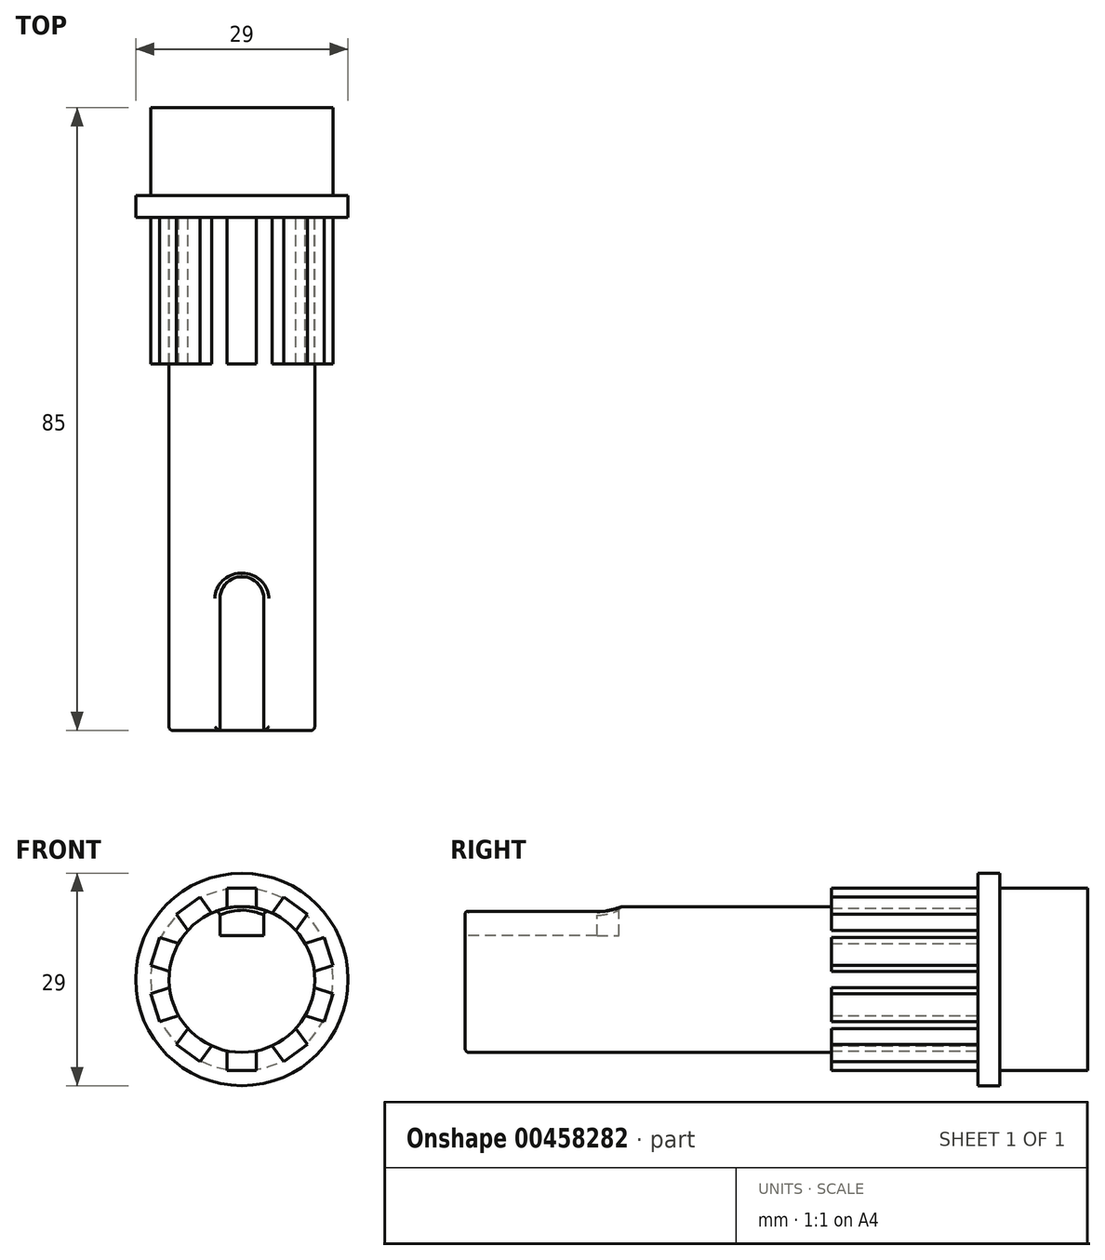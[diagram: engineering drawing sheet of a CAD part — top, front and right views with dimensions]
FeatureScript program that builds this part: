
annotation { "Feature Type Name" : "Feature", "Feature Type Description" : "" }
export const myFeature = defineFeature(function(context is Context, id is Id, definition is map)
    precondition{}
    {
        {
            var Q0;
            Q0=qCreatedBy(makeId("Front.planeOp"),FACE);
            var sketch = newSketch(context, id + "F0", { "sketchPlane" : qUnion([Q0])});
            skCircle(sketch, "E0", {"center": v(0, 0) * mm, "radius": 12.45 * mm});
            skSolve(sketch);
        }
        {
            var Q0;
            Q0=makeQuery(id+"F0.imprint","IMPRINT",FACE,{"disambiguationData":[TD([[makeQuery(id+"F0.imprint","IMPRINT",EDGE,{"derivedFrom":sQuery(id+"F0.wireOp",EDGE,"E0")}),1.0]])]});
            extrude(context, id + "F1", {"entities" : qUnion([Q0]), "oppositeDirection" : true, "depth" : 12 * mm, "offsetDistance" : 25 * mm});
        }
        {
            var Q0;
            Q0=qCreatedBy(makeId("Front.planeOp"),FACE);
            var sketch = newSketch(context, id + "F2", { "sketchPlane" : qUnion([Q0])});
            skCircle(sketch, "E1", {"center": v(0, 0) * mm, "radius": 14.5 * mm});
            skSolve(sketch);
        }
        {
            var Q0;
            Q0=makeQuery(id+"F2.imprint","IMPRINT",FACE,{"disambiguationData":[TD([[makeQuery(id+"F2.imprint","IMPRINT",EDGE,{"derivedFrom":sQuery(id+"F2.wireOp",EDGE,"E1")}),1.0]])]});
            extrude(context, id + "F3", {"entities" : qUnion([Q0]), "operationType" : NewBodyOperationType.ADD, "depth" : 3 * mm, "offsetDistance" : 25 * mm});
        }
        {
            var Q0;
            Q0=qCreatedBy(makeId("Front.planeOp"),FACE);
            cPlane(context, id + "F4", {"entities" : qUnion([Q0]), "cplaneType" : CPlaneType.OFFSET, "offset" : 3 * mm, "width" : 150 * mm, "height" : 150 * mm});
        }
        {
            var Q0;
            Q0=qCreatedBy(id+"F4.planeOp",FACE);
            var sketch = newSketch(context, id + "F5", { "sketchPlane" : qUnion([Q0])});
            skCircle(sketch, "E2", {"center": v(0, 0) * mm, "radius": 9.95 * mm});
            skSolve(sketch);
        }
        {
            var Q0;
            Q0=makeQuery(id+"F5.imprint","IMPRINT",FACE,{"disambiguationData":[TD([[makeQuery(id+"F5.imprint","IMPRINT",EDGE,{"derivedFrom":sQuery(id+"F5.wireOp",EDGE,"E2")}),1.0]])]});
            extrude(context, id + "F6", {"entities" : qUnion([Q0]), "operationType" : NewBodyOperationType.ADD, "depth" : 70 * mm});
        }
        {
            var Q0;
            Q0=qCreatedBy(id+"F4.planeOp",FACE);
            var sketch = newSketch(context, id + "F7", { "sketchPlane" : qUnion([Q0])});
            skLineSegment(sketch, "E3.bottom", {"start": v(2, 12.45) * mm, "end": v(-2, 12.45) * mm});
            skLineSegment(sketch, "E3.top", {"start": v(2, 7.45) * mm, "end": v(-2, 7.45) * mm});
            skLineSegment(sketch, "E3.left", {"start": v(2, 12.45) * mm, "end": v(2, 7.45) * mm});
            skLineSegment(sketch, "E3.right", {"start": v(-2, 12.45) * mm, "end": v(-2, 7.45) * mm});
            skPoint(sketch, "E3.middle", {"position": v(0, 9.95) * mm});
            skLineSegment(sketch, "E4.1.0", {"start": v(-2.76, 7.2) * mm, "end": v(-6, 4.85) * mm});
            skLineSegment(sketch, "E4.1.1", {"start": v(-5.7, 11.25) * mm, "end": v(-8.94, 8.9) * mm});
            skPoint(sketch, "E4.1.2", {"position": v(-5.85, 8.05) * mm});
            skLineSegment(sketch, "E4.1.3", {"start": v(-8.94, 8.9) * mm, "end": v(-6, 4.85) * mm});
            skLineSegment(sketch, "E4.1.4", {"start": v(-5.7, 11.25) * mm, "end": v(-2.76, 7.2) * mm});
            skLineSegment(sketch, "E4.2.0", {"start": v(-6.47, 4.2) * mm, "end": v(-7.7, 0.4) * mm});
            skLineSegment(sketch, "E4.2.1", {"start": v(-11.22, 5.75) * mm, "end": v(-12.46, 1.95) * mm});
            skPoint(sketch, "E4.2.2", {"position": v(-9.46, 3.08) * mm});
            skLineSegment(sketch, "E4.2.3", {"start": v(-12.46, 1.95) * mm, "end": v(-7.7, 0.4) * mm});
            skLineSegment(sketch, "E4.2.4", {"start": v(-11.22, 5.75) * mm, "end": v(-6.47, 4.2) * mm});
            skLineSegment(sketch, "E4.3.0", {"start": v(-7.7, -0.4) * mm, "end": v(-6.47, -4.2) * mm});
            skLineSegment(sketch, "E4.3.1", {"start": v(-12.46, -1.95) * mm, "end": v(-11.22, -5.75) * mm});
            skPoint(sketch, "E4.3.2", {"position": v(-9.46, -3.08) * mm});
            skLineSegment(sketch, "E4.3.3", {"start": v(-11.22, -5.75) * mm, "end": v(-6.47, -4.2) * mm});
            skLineSegment(sketch, "E4.3.4", {"start": v(-12.46, -1.95) * mm, "end": v(-7.7, -0.4) * mm});
            skLineSegment(sketch, "E4.4.0", {"start": v(-6, -4.85) * mm, "end": v(-2.76, -7.2) * mm});
            skLineSegment(sketch, "E4.4.1", {"start": v(-8.94, -8.9) * mm, "end": v(-5.7, -11.25) * mm});
            skPoint(sketch, "E4.4.2", {"position": v(-5.85, -8.05) * mm});
            skLineSegment(sketch, "E4.4.3", {"start": v(-5.7, -11.25) * mm, "end": v(-2.76, -7.2) * mm});
            skLineSegment(sketch, "E4.4.4", {"start": v(-8.94, -8.9) * mm, "end": v(-6, -4.85) * mm});
            skLineSegment(sketch, "E4.5.0", {"start": v(-2, -7.45) * mm, "end": v(2, -7.45) * mm});
            skLineSegment(sketch, "E4.5.1", {"start": v(-2, -12.45) * mm, "end": v(2, -12.45) * mm});
            skPoint(sketch, "E4.5.2", {"position": v(0, -9.95) * mm});
            skLineSegment(sketch, "E4.5.3", {"start": v(2, -12.45) * mm, "end": v(2, -7.45) * mm});
            skLineSegment(sketch, "E4.5.4", {"start": v(-2, -12.45) * mm, "end": v(-2, -7.45) * mm});
            skLineSegment(sketch, "E4.6.0", {"start": v(2.76, -7.2) * mm, "end": v(6, -4.85) * mm});
            skLineSegment(sketch, "E4.6.1", {"start": v(5.7, -11.25) * mm, "end": v(8.94, -8.9) * mm});
            skPoint(sketch, "E4.6.2", {"position": v(5.85, -8.05) * mm});
            skLineSegment(sketch, "E4.6.3", {"start": v(8.94, -8.9) * mm, "end": v(6, -4.85) * mm});
            skLineSegment(sketch, "E4.6.4", {"start": v(5.7, -11.25) * mm, "end": v(2.76, -7.2) * mm});
            skLineSegment(sketch, "E4.7.0", {"start": v(6.47, -4.2) * mm, "end": v(7.7, -0.4) * mm});
            skLineSegment(sketch, "E4.7.1", {"start": v(11.22, -5.75) * mm, "end": v(12.46, -1.95) * mm});
            skPoint(sketch, "E4.7.2", {"position": v(9.46, -3.08) * mm});
            skLineSegment(sketch, "E4.7.3", {"start": v(12.46, -1.95) * mm, "end": v(7.7, -0.4) * mm});
            skLineSegment(sketch, "E4.7.4", {"start": v(11.22, -5.75) * mm, "end": v(6.47, -4.2) * mm});
            skLineSegment(sketch, "E4.8.0", {"start": v(7.7, 0.4) * mm, "end": v(6.47, 4.2) * mm});
            skLineSegment(sketch, "E4.8.1", {"start": v(12.46, 1.95) * mm, "end": v(11.22, 5.75) * mm});
            skPoint(sketch, "E4.8.2", {"position": v(9.46, 3.08) * mm});
            skLineSegment(sketch, "E4.8.3", {"start": v(11.22, 5.75) * mm, "end": v(6.47, 4.2) * mm});
            skLineSegment(sketch, "E4.8.4", {"start": v(12.46, 1.95) * mm, "end": v(7.7, 0.4) * mm});
            skLineSegment(sketch, "E4.9.0", {"start": v(6, 4.85) * mm, "end": v(2.76, 7.2) * mm});
            skLineSegment(sketch, "E4.9.1", {"start": v(8.94, 8.9) * mm, "end": v(5.7, 11.25) * mm});
            skPoint(sketch, "E4.9.2", {"position": v(5.85, 8.05) * mm});
            skLineSegment(sketch, "E4.9.3", {"start": v(5.7, 11.25) * mm, "end": v(2.76, 7.2) * mm});
            skLineSegment(sketch, "E4.9.4", {"start": v(8.94, 8.9) * mm, "end": v(6, 4.85) * mm});
            skPoint(sketch, "E4.center", {"position": v(0, 0) * mm});
            skSolve(sketch);
        }
        {
            var Q0;
            Q0=makeQuery(id+"F7.imprint","IMPRINT",FACE,{"disambiguationData":[TD([[makeQuery(id+"F7.imprint","IMPRINT",EDGE,{"derivedFrom":sQuery(id+"F7.wireOp",EDGE,"E3.bottom")}),1.0]])]});
            var Q1;
            Q1=makeQuery(id+"F7.imprint","IMPRINT",FACE,{"disambiguationData":[TD([[makeQuery(id+"F7.imprint","IMPRINT",EDGE,{"derivedFrom":sQuery(id+"F7.wireOp",EDGE,"E4.9.0")}),-1.0]])]});
            var Q2;
            Q2=makeQuery(id+"F7.imprint","IMPRINT",FACE,{"disambiguationData":[TD([[makeQuery(id+"F7.imprint","IMPRINT",EDGE,{"derivedFrom":sQuery(id+"F7.wireOp",EDGE,"E4.8.0")}),-1.0]])]});
            var Q3;
            Q3=makeQuery(id+"F7.imprint","IMPRINT",FACE,{"disambiguationData":[TD([[makeQuery(id+"F7.imprint","IMPRINT",EDGE,{"derivedFrom":sQuery(id+"F7.wireOp",EDGE,"E4.7.0")}),-1.0]])]});
            var Q4;
            Q4=makeQuery(id+"F7.imprint","IMPRINT",FACE,{"disambiguationData":[TD([[makeQuery(id+"F7.imprint","IMPRINT",EDGE,{"derivedFrom":sQuery(id+"F7.wireOp",EDGE,"E4.6.0")}),-1.0]])]});
            var Q5;
            Q5=makeQuery(id+"F7.imprint","IMPRINT",FACE,{"disambiguationData":[TD([[makeQuery(id+"F7.imprint","IMPRINT",EDGE,{"derivedFrom":sQuery(id+"F7.wireOp",EDGE,"E4.5.0")}),-1.0]])]});
            var Q6;
            Q6=makeQuery(id+"F7.imprint","IMPRINT",FACE,{"disambiguationData":[TD([[makeQuery(id+"F7.imprint","IMPRINT",EDGE,{"derivedFrom":sQuery(id+"F7.wireOp",EDGE,"E4.4.0")}),-1.0]])]});
            var Q7;
            Q7=makeQuery(id+"F7.imprint","IMPRINT",FACE,{"disambiguationData":[TD([[makeQuery(id+"F7.imprint","IMPRINT",EDGE,{"derivedFrom":sQuery(id+"F7.wireOp",EDGE,"E4.3.0")}),-1.0]])]});
            var Q8;
            Q8=makeQuery(id+"F7.imprint","IMPRINT",FACE,{"disambiguationData":[TD([[makeQuery(id+"F7.imprint","IMPRINT",EDGE,{"derivedFrom":sQuery(id+"F7.wireOp",EDGE,"E4.2.0")}),-1.0]])]});
            var Q9;
            Q9=makeQuery(id+"F7.imprint","IMPRINT",FACE,{"disambiguationData":[TD([[makeQuery(id+"F7.imprint","IMPRINT",EDGE,{"derivedFrom":sQuery(id+"F7.wireOp",EDGE,"E4.1.0")}),-1.0]])]});
            extrude(context, id + "F8", {"entities" : qUnion([Q0, Q1, Q2, Q3, Q4, Q5, Q6, Q7, Q8, Q9]), "operationType" : NewBodyOperationType.ADD, "depth" : 20 * mm, "offsetDistance" : 25 * mm});
        }
        {
            var Q0;
            Q0=qCreatedBy(makeId("Front.planeOp"),FACE);
            cPlane(context, id + "F9", {"entities" : qUnion([Q0]), "cplaneType" : CPlaneType.OFFSET, "offset" : 73 * mm, "width" : 150 * mm, "height" : 150 * mm});
        }
        {
            var Q0;
            Q0=qCreatedBy(id+"F9.planeOp",FACE);
            var sketch = newSketch(context, id + "F10", { "sketchPlane" : qUnion([Q0])});
            skLineSegment(sketch, "E5.bottom", {"start": v(3, 6) * mm, "end": v(-3, 6) * mm});
            skLineSegment(sketch, "E5.top", {"start": v(3, 11) * mm, "end": v(-3, 11) * mm});
            skLineSegment(sketch, "E5.left", {"start": v(3, 6) * mm, "end": v(3, 11) * mm});
            skLineSegment(sketch, "E5.right", {"start": v(-3, 6) * mm, "end": v(-3, 11) * mm});
            skPoint(sketch, "E5.middle", {"position": v(0, 8.5) * mm});
            skSolve(sketch);
        }
        {
            var Q0;
            Q0=makeQuery(id+"F10.imprint","IMPRINT",FACE,{"disambiguationData":[TD([[makeQuery(id+"F10.imprint","IMPRINT",EDGE,{"derivedFrom":sQuery(id+"F10.wireOp",EDGE,"E5.bottom")}),-1.0]])]});
            extrude(context, id + "F11", {"entities" : qUnion([Q0]), "operationType" : NewBodyOperationType.REMOVE, "oppositeDirection" : true, "depth" : 18 * mm});
        }
        {
            var Q0;
            Q0=qCreatedBy(makeId("Top.planeOp"),FACE);
            cPlane(context, id + "F12", {"entities" : qUnion([Q0]), "cplaneType" : CPlaneType.OFFSET, "offset" : 10 * mm, "width" : 150 * mm, "height" : 150 * mm});
        }
        {
            var Q0;
            Q0=qCreatedBy(id+"F12.planeOp",FACE);
            var sketch = newSketch(context, id + "F13", { "sketchPlane" : qUnion([Q0])});
            skCircle(sketch, "E6", {"center": v(0, -55.02) * mm, "radius": 3 * mm});
            skSolve(sketch);
        }
        {
            var Q0;
            Q0=makeQuery(id+"F13.imprint","IMPRINT",FACE,{"disambiguationData":[TD([[makeQuery(id+"F13.imprint","IMPRINT",EDGE,{"derivedFrom":sQuery(id+"F13.wireOp",EDGE,"E6")}),1.0]])]});
            var Q1;
            Q1=makeQuery(id+"F11.boolean.opBoolean","COPY",FACE,{"derivedFrom":makeQuery(id+"F11.opExtrude","SWEPT_FACE",FACE,{"disambiguationData":[OSD([sQuery(id+"F10.wireOp",EDGE,"E5.bottom")])]})});
            extrude(context, id + "F14", {"entities" : qUnion([Q0]), "operationType" : NewBodyOperationType.REMOVE, "endBound" : BoundingType.UP_TO_SURFACE, "oppositeDirection" : true, "endBoundEntityFace" : qUnion([Q1]), "depth" : 25 * mm});
        }
        {
            var Q0;
            Q0=makeQuery(id+"F6.opExtrude","CAP_EDGE",EDGE,{"disambiguationData":[OSD([sQuery(id+"F5.wireOp",EDGE,"E2")])],"isStart":false});
            var Q1;
            Q1=makeQuery(id+"F11.boolean.opBoolean","INTERSECT",EDGE,{"derivedFrom":[makeQuery(id+"F6.opExtrude","SWEPT_FACE",FACE,{"disambiguationData":[OSD([sQuery(id+"F5.wireOp",EDGE,"E2")])]}),makeQuery(id+"F11.opExtrude","SWEPT_FACE",FACE,{"disambiguationData":[OSD([sQuery(id+"F10.wireOp",EDGE,"E5.right")])]})]});
            var Q2;
            Q2=makeQuery(id+"F14.boolean.opBoolean","INTERSECT",EDGE,{"derivedFrom":[makeQuery(id+"F6.opExtrude","SWEPT_FACE",FACE,{"disambiguationData":[OSD([sQuery(id+"F5.wireOp",EDGE,"E2")])]}),makeQuery(id+"F14.opExtrude","SWEPT_FACE",FACE,{"disambiguationData":[OSD([sQuery(id+"F13.wireOp",EDGE,"E6")])]})]});
            var Q3;
            Q3=makeQuery(id+"F11.boolean.opBoolean","INTERSECT",EDGE,{"derivedFrom":[makeQuery(id+"F6.opExtrude","SWEPT_FACE",FACE,{"disambiguationData":[OSD([sQuery(id+"F5.wireOp",EDGE,"E2")])]}),makeQuery(id+"F11.opExtrude","SWEPT_FACE",FACE,{"disambiguationData":[OSD([sQuery(id+"F10.wireOp",EDGE,"E5.left")])]})]});
            fillet(context, id + "F15", {"entities" : qUnion([Q0, Q1, Q2, Q3]), "radius" : .5 * mm, "tangentPropagation" : true, "allowEdgeOverflow" : false});
        }
    });
